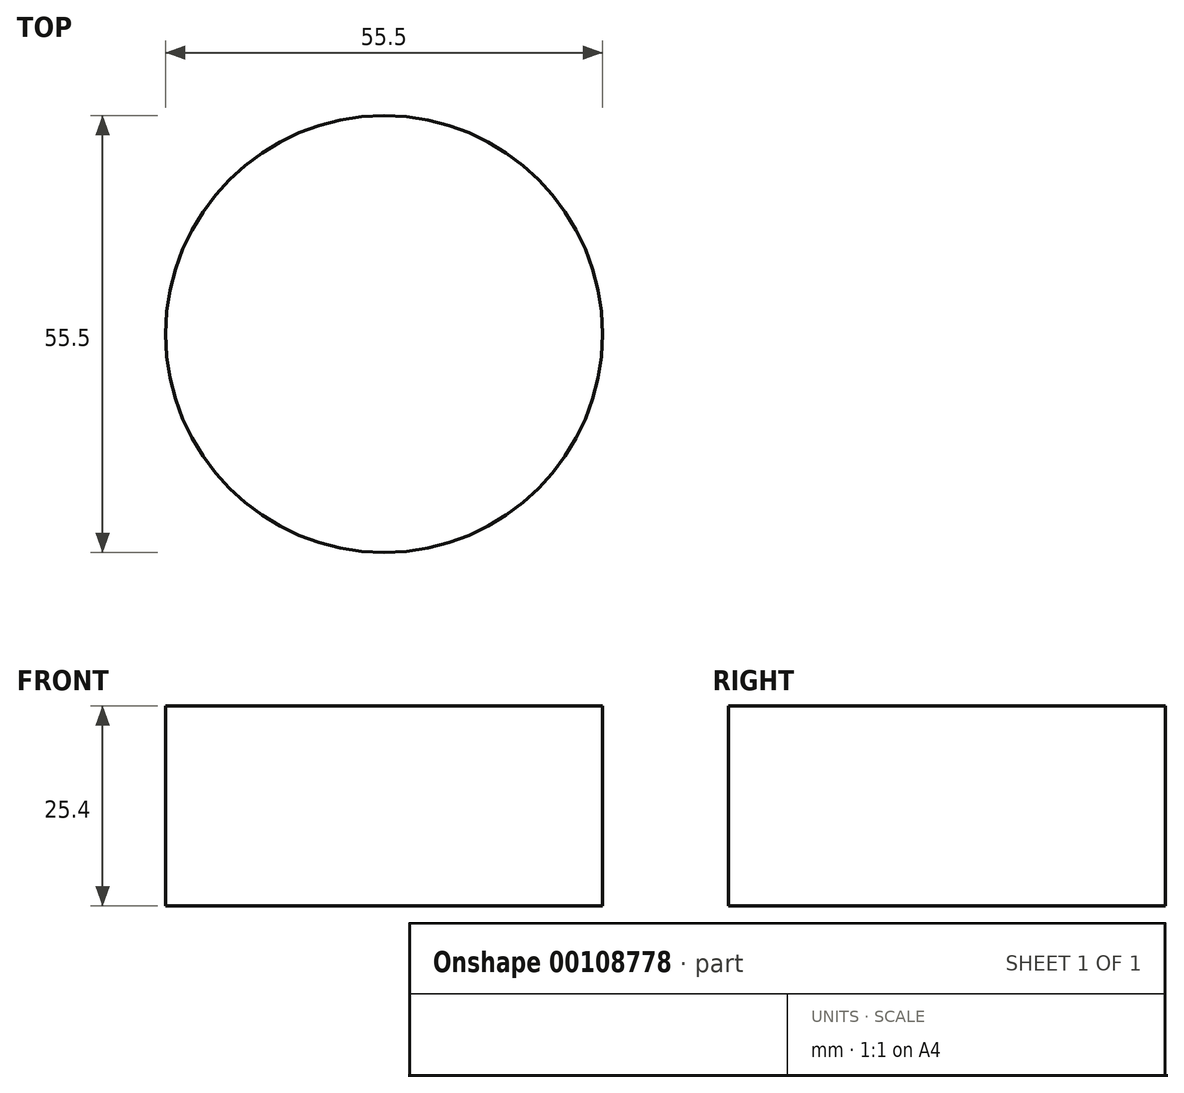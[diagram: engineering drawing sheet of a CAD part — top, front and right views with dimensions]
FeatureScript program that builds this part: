
annotation { "Feature Type Name" : "Feature", "Feature Type Description" : "" }
export const myFeature = defineFeature(function(context is Context, id is Id, definition is map)
    precondition{}
    {
        {
            var Q0;
            Q0=qCreatedBy(makeId("Top.planeOp"),FACE);
            var sketch = newSketch(context, id + "F0", { "sketchPlane" : qUnion([Q0])});
            skCircle(sketch, "E0", {"center": v(0, 0) * mm, "radius": 27.75 * mm});
            skSolve(sketch);
        }
        {
            var Q0;
            Q0=makeQuery(id+"F0.imprint","IMPRINT",FACE,{"disambiguationData":[TD([[makeQuery(id+"F0.imprint","IMPRINT",EDGE,{"derivedFrom":sQuery(id+"F0.wireOp",EDGE,"E0")}),1.0]])]});
            extrude(context, id + "F1", {"entities" : qUnion([Q0]), "depth" : 25.4 * mm});
        }
    });
